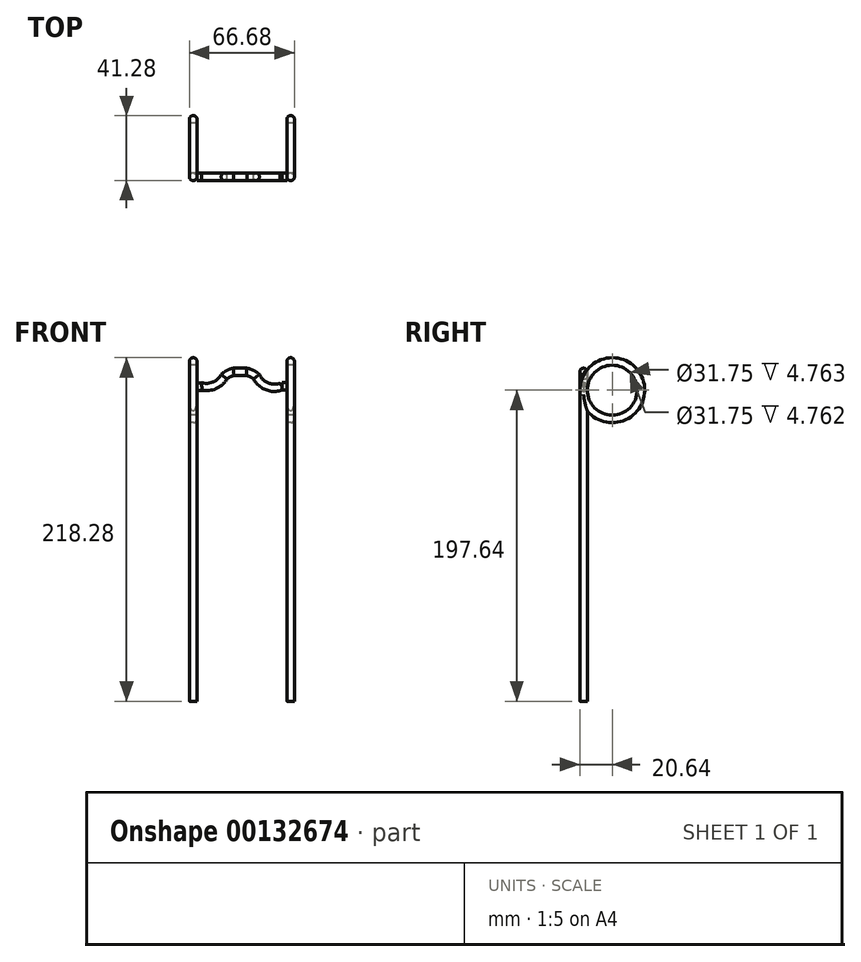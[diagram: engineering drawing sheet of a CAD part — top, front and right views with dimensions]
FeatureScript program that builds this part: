
annotation { "Feature Type Name" : "Feature", "Feature Type Description" : "" }
export const myFeature = defineFeature(function(context is Context, id is Id, definition is map)
    precondition{}
    {
        {
            var Q0;
            Q0=qCreatedBy(makeId("Right.planeOp"),FACE);
            var sketch = newSketch(context, id + "F0", { "sketchPlane" : qUnion([Q0])});
            skCircle(sketch, "E0", {"center": v(0, 0) * mm, "radius": 15.88 * mm});
            skLineSegment(sketch, "E1.bottom", {"start": v(-15.88, 0) * mm, "end": v(-20.64, 0) * mm});
            skLineSegment(sketch, "E1.top", {"start": v(-15.87, -197.64) * mm, "end": v(-20.64, -197.64) * mm});
            skLineSegment(sketch, "E1.left", {"start": v(-15.88, 0) * mm, "end": v(-15.87, -197.64) * mm});
            skLineSegment(sketch, "E1.right", {"start": v(-20.64, 0) * mm, "end": v(-20.64, -197.64) * mm});
            skCircle(sketch, "E2", {"center": v(0, 0) * mm, "radius": 20.64 * mm});
            skSolve(sketch);
        }
        {
            var Q0;
            {var subQ0=sQuery(id+"F0.wireOp",EDGE,"E1.top");Q0=makeQuery(id+"F0.imprint","IMPRINT",FACE,{"disambiguationData":[TD([[makeQuery(id+"F0.imprint","IMPRINT",EDGE,{"derivedFrom":subQ0}),-1.0]])]});}
            var Q1;
            {var subQ0=sQuery(id+"F0.wireOp",EDGE,"E1.bottom");Q1=makeQuery(id+"F0.imprint","IMPRINT",FACE,{"disambiguationData":[TD([[makeQuery(id+"F0.imprint","IMPRINT",EDGE,{"derivedFrom":subQ0}),1.0]])]});}
            var Q2;
            {var subQ0=sQuery(id+"F0.wireOp",EDGE,"E0");Q2=makeQuery(id+"F0.imprint","IMPRINT",FACE,{"disambiguationData":[TD([[makeQuery(id+"F0.imprint","IMPRINT",EDGE,{"derivedFrom":subQ0}),-1.0]])]});}
            extrude(context, id + "F1", {"entities" : qUnion([Q0, Q1, Q2]), "depth" : 4.76 * mm});
        }
        {
            var Q0;
            Q0=makeQuery(id+"F1.opExtrude","CAP_EDGE",EDGE,{"disambiguationData":[OSD([sQuery(id+"F0.wireOp",EDGE,"E1.right")])],"isStart":true});
            var Q1;
            Q1=makeQuery(id+"F1.opExtrude","CAP_EDGE",EDGE,{"disambiguationData":[OSD([sQuery(id+"F0.wireOp",EDGE,"E1.left")])],"isStart":true});
            var Q2;
            Q2=makeQuery(id+"F1.opExtrude","CAP_EDGE",EDGE,{"disambiguationData":[OSD([sQuery(id+"F0.wireOp",EDGE,"E1.left")])],"isStart":false});
            var Q3;
            Q3=makeQuery(id+"F1.opExtrude","CAP_EDGE",EDGE,{"disambiguationData":[OSD([sQuery(id+"F0.wireOp",EDGE,"E1.right")])],"isStart":false});
            fillet(context, id + "F2", {"entities" : qUnion([Q0, Q1, Q2, Q3]), "radius" : 2.3 * mm, "tangentPropagation" : true, "allowEdgeOverflow" : false});
        }
        {
            var Q0;
            Q0=makeQuery(id+"F1.opExtrude","SWEPT_BODY",BODY,{"disambiguationData":[OSD([sQuery(id+"F0.wireOp",EDGE,"E0"),sQuery(id+"F0.wireOp",EDGE,"E1.top"),sQuery(id+"F0.wireOp",EDGE,"E1.left"),sQuery(id+"F0.wireOp",EDGE,"E1.right"),sQuery(id+"F0.wireOp",EDGE,"E2")])]});
            transform(context, id + "F3", {"entities" : qUnion([Q0]), "transformType" : TransformType.TRANSLATION_3D, "dx" : 61.9 * mm, "dy" : 0 * mm, "dz" : 0 * mm, "makeCopy" : true});
        }
        {
            var Q0;
            Q0=makeQuery(id+"F1.opExtrude","CAP_FACE",FACE,{"disambiguationData":[OSD([sQuery(id+"F0.wireOp",EDGE,"E0"),sQuery(id+"F0.wireOp",EDGE,"E1.top"),sQuery(id+"F0.wireOp",EDGE,"E1.left"),sQuery(id+"F0.wireOp",EDGE,"E1.right"),sQuery(id+"F0.wireOp",EDGE,"E2")])],"isStart":false});
            var sketch = newSketch(context, id + "F4", { "sketchPlane" : qUnion([Q0])});
            skLineSegment(sketch, "E3.top", {"start": v(-14.96, 0) * mm, "end": v(-10.2, 0) * mm});
            skCircle(sketch, "E4", {"center": v(-18.2, 2.33) * mm, "radius": 2.38 * mm});
            skPoint(sketch, "E4.centerSnap0", {"position": v(-14.96, 2.33) * mm});
            skPoint(sketch, "E4.centerSnap1", {"position": v(-18.2, 4.76) * mm});
            skSolve(sketch);
        }
        {
            var Q0;
            Q0=makeQuery(id+"F3.opPattern","COPY",FACE,{"derivedFrom":makeQuery(id+"F1.opExtrude","CAP_FACE",FACE,{"disambiguationData":[OSD([sQuery(id+"F0.wireOp",EDGE,"E0"),sQuery(id+"F0.wireOp",EDGE,"E1.top"),sQuery(id+"F0.wireOp",EDGE,"E1.left"),sQuery(id+"F0.wireOp",EDGE,"E1.right"),sQuery(id+"F0.wireOp",EDGE,"E2")])],"isStart":true}),"instanceName":"1"});
            var sketch = newSketch(context, id + "F5", { "sketchPlane" : qUnion([Q0])});
            skCircle(sketch, "E5", {"center": v(18.2, 2.37) * mm, "radius": 2.38 * mm});
            skSolve(sketch);
        }
        {
            var Q0;
            {var subQ0=sQuery(id+"F4.wireOp",EDGE,"E4");var subQ1=sQuery(id+"F0.wireOp",EDGE,"E2");var subQ2=makeQuery(id+"F2.opFillet","BLEND_EDGE",EDGE,{"blendedFrom":[makeQuery(id+"F1.opExtrude","CAP_EDGE",EDGE,{"disambiguationData":[OSD([subQ1])],"isStart":false}),makeQuery(id+"F1.opExtrude","CAP_FACE",FACE,{"disambiguationData":[OSD([sQuery(id+"F0.wireOp",EDGE,"E0"),sQuery(id+"F0.wireOp",EDGE,"E1.top"),sQuery(id+"F0.wireOp",EDGE,"E1.left"),sQuery(id+"F0.wireOp",EDGE,"E1.right"),subQ1])],"isStart":false})],"blendedInto":[makeQuery(id+"F1.opExtrude","CAP_FACE",FACE,{"disambiguationData":[OSD([sQuery(id+"F0.wireOp",EDGE,"E0"),sQuery(id+"F0.wireOp",EDGE,"E1.top"),sQuery(id+"F0.wireOp",EDGE,"E1.left"),sQuery(id+"F0.wireOp",EDGE,"E1.right"),subQ1])],"isStart":false})]});var subQ3=makeQuery(id+"F4.imprint","INTERSECT",VERTEX,{"disambiguationData":[OD(0.0)],"derivedFrom":[subQ2,subQ0]});Q0=makeQuery(id+"F4.imprint","IMPRINT",FACE,{"disambiguationData":[TD([[makeQuery(id+"F4.imprint","IMPRINT",EDGE,{"disambiguationData":[TD([[subQ3,1.0]])],"derivedFrom":subQ0}),1.0]])]});}
            var Q1;
            {var subQ0=sQuery(id+"F4.wireOp",EDGE,"E4");var subQ1=makeQuery(id+"F4.imprint","INTERSECT",VERTEX,{"derivedFrom":[sQuery(id+"F4.wireOp",EDGE,"E3.top"),subQ0]});Q1=makeQuery(id+"F4.imprint","IMPRINT",FACE,{"disambiguationData":[TD([[makeQuery(id+"F4.imprint","IMPRINT",EDGE,{"disambiguationData":[TD([[subQ1,1.0]])],"derivedFrom":subQ0}),1.0]])]});}
            extrude(context, id + "F6", {"entities" : qUnion([Q0, Q1]), "operationType" : NewBodyOperationType.ADD, "depth" : 3.17 * mm});
        }
        {
            var Q0;
            {var subQ0=sQuery(id+"F5.wireOp",EDGE,"E5");var subQ1=sQuery(id+"F0.wireOp",EDGE,"E2");var subQ2=makeQuery(id+"F3.opPattern","COPY",EDGE,{"derivedFrom":makeQuery(id+"F2.opFillet","BLEND_EDGE",EDGE,{"blendedFrom":[makeQuery(id+"F1.opExtrude","CAP_EDGE",EDGE,{"disambiguationData":[OSD([subQ1])],"isStart":true}),makeQuery(id+"F1.opExtrude","CAP_FACE",FACE,{"disambiguationData":[OSD([sQuery(id+"F0.wireOp",EDGE,"E0"),sQuery(id+"F0.wireOp",EDGE,"E1.top"),sQuery(id+"F0.wireOp",EDGE,"E1.left"),sQuery(id+"F0.wireOp",EDGE,"E1.right"),subQ1])],"isStart":true})],"blendedInto":[makeQuery(id+"F1.opExtrude","CAP_FACE",FACE,{"disambiguationData":[OSD([sQuery(id+"F0.wireOp",EDGE,"E0"),sQuery(id+"F0.wireOp",EDGE,"E1.top"),sQuery(id+"F0.wireOp",EDGE,"E1.left"),sQuery(id+"F0.wireOp",EDGE,"E1.right"),subQ1])],"isStart":true})]}),"instanceName":"1"});var subQ3=makeQuery(id+"F5.imprint","INTERSECT",VERTEX,{"disambiguationData":[OD(0.0)],"derivedFrom":[subQ2,subQ0]});Q0=makeQuery(id+"F5.imprint","IMPRINT",FACE,{"disambiguationData":[TD([[makeQuery(id+"F5.imprint","IMPRINT",EDGE,{"disambiguationData":[TD([[subQ3,1.0]])],"derivedFrom":subQ0}),1.0]])]});}
            var Q1;
            {var subQ0=sQuery(id+"F5.wireOp",EDGE,"E5");var subQ1=sQuery(id+"F0.wireOp",EDGE,"E2");var subQ2=makeQuery(id+"F3.opPattern","COPY",EDGE,{"derivedFrom":makeQuery(id+"F2.opFillet","BLEND_EDGE",EDGE,{"blendedFrom":[makeQuery(id+"F1.opExtrude","CAP_EDGE",EDGE,{"disambiguationData":[OSD([subQ1])],"isStart":true}),makeQuery(id+"F1.opExtrude","CAP_FACE",FACE,{"disambiguationData":[OSD([sQuery(id+"F0.wireOp",EDGE,"E0"),sQuery(id+"F0.wireOp",EDGE,"E1.top"),sQuery(id+"F0.wireOp",EDGE,"E1.left"),sQuery(id+"F0.wireOp",EDGE,"E1.right"),subQ1])],"isStart":true})],"blendedInto":[makeQuery(id+"F1.opExtrude","CAP_FACE",FACE,{"disambiguationData":[OSD([sQuery(id+"F0.wireOp",EDGE,"E0"),sQuery(id+"F0.wireOp",EDGE,"E1.top"),sQuery(id+"F0.wireOp",EDGE,"E1.left"),sQuery(id+"F0.wireOp",EDGE,"E1.right"),subQ1])],"isStart":true})]}),"instanceName":"1"});var subQ3=makeQuery(id+"F5.imprint","INTERSECT",VERTEX,{"disambiguationData":[OD(0.0)],"derivedFrom":[subQ2,subQ0]});Q1=makeQuery(id+"F5.imprint","IMPRINT",FACE,{"disambiguationData":[TD([[makeQuery(id+"F5.imprint","IMPRINT",EDGE,{"disambiguationData":[TD([[subQ3,-1.0]])],"derivedFrom":subQ0}),1.0]])]});}
            extrude(context, id + "F7", {"entities" : qUnion([Q0, Q1]), "operationType" : NewBodyOperationType.ADD, "depth" : 3.17 * mm});
        }
        {
            var Q0;
            Q0=qCreatedBy(makeId("Front.planeOp"),FACE);
            var sketch = newSketch(context, id + "F8", { "sketchPlane" : qUnion([Q0])});
            skArc(sketch, "E6", {"start": v(7.8, 2.62) * mm, "mid": v(15.8, 3.31) * mm, "end": v(21.79, 8.68) * mm});
            skArc(sketch, "E7", {"start": v(42.73, 8.68) * mm, "mid": v(49.5, 2.6) * mm, "end": v(58.6, 2.62) * mm});
            skLineSegment(sketch, "E8", {"start": v(71.44, -6.09) * mm, "end": v(71.64, -5.68) * mm});
            skArc(sketch, "E9", {"start": v(28.05, 11.88) * mm, "mid": v(24.7, 10.72) * mm, "end": v(21.79, 8.68) * mm});
            skArc(sketch, "E10", {"start": v(42.73, 8.68) * mm, "mid": v(39.75, 10.75) * mm, "end": v(36.3, 11.88) * mm});
            skLineSegment(sketch, "E11", {"start": v(28.05, 11.88) * mm, "end": v(36.3, 11.88) * mm});
            skSolve(sketch);
        }
        {
            var Q0;
            Q0=makeQuery(id+"F6.opExtrude","CAP_FACE",FACE,{"disambiguationData":[OSD([sQuery(id+"F4.wireOp",EDGE,"E4")])],"isStart":false});
            var Q1;
            Q1=qSketchRegion(id+"F8",true);
            var Q2;
            Q2=sQuery(id+"F8.wireOp",EDGE,"E6");
            var Q3;
            Q3=sQuery(id+"F8.wireOp",EDGE,"E9");
            var Q4;
            Q4=sQuery(id+"F8.wireOp",EDGE,"E11");
            var Q5;
            Q5=sQuery(id+"F8.wireOp",EDGE,"E10");
            var Q6;
            Q6=sQuery(id+"F8.wireOp",EDGE,"E7");
            sweep(context, id + "F9", {"operationType" : NewBodyOperationType.ADD, "profiles" : qUnion([Q0, Q1]), "path" : qUnion([Q2, Q3, Q4, Q5, Q6])});
        }
    });
